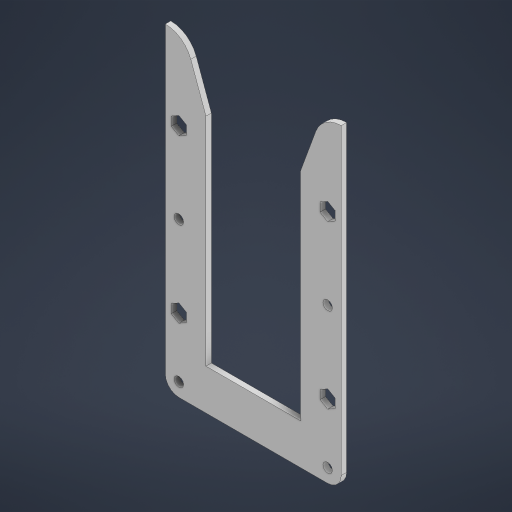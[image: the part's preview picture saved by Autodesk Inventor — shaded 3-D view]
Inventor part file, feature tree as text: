
AUTODESK INVENTOR PART (.ipt)
format: ipt  version: 2023 (Build 270158000, 158)  size: 223,232 bytes
history: native  units: mm
features: other x3, plane x1, extrude x1, sketch x1, reference x1
ambient origin geometry x8: Origin, YZ Plane, XZ Plane, XY Plane, X Axis, Y Axis, Z Axis, Center Point
bodies: Solid1 (feature_tree)
feature tree (7):
  plane  "Work Plane1"
  extrude  "Extrusion1"  Depth=5.0mm
  sketch  "Sketch1"  dims[d0=5.0mm d1=5.0mm d2=5.0mm d3=3.490659mm d5=2.0mm d6=0.0mm]
  reference  "Reference1"
  parser-record x1  (decoder bookkeeping rows leaked as tree rows — omitted from the tree; the rows remain in map.json)
  other  "total.iam"
  other  "middle spacer top:1"
note: 1 file-system path scrubbed to <path> (originals preserved in map.json)
